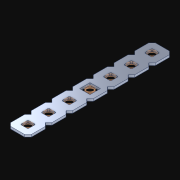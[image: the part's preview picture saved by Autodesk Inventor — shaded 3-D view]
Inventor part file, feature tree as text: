
AUTODESK INVENTOR PART (.ipt)
format: ipt  version: 2021 (Build 250183000, 183)  size: 206,336 bytes
history: native  units: in
note: dims shown in document units (in); Inventor stores cm internally (conversion verified against a paired STEP export)
features: other x8, extrude x7, pattern_linear x1, sketch x1
ambient origin geometry x8: Origin, YZ Plane, XZ Plane, XY Plane, X Axis, Y Axis, Z Axis, Center Point
bodies: Solid1 (feature_tree)
feature tree (17):
  pattern_linear  "Rectangular Pattern1"  Spacing1=1.0in  [1 undecoded]
  sketch  "Sketch1"  dims[d0=0.182in d1=1.0in d2=0.0in d3=2.7559in d5=0.5in]
  other  "Srf1"
  other  "Srf2"
  other  "Srf3"
  other  "Srf4"
  other  "Srf5"
  other  "Srf6"
  other  "Srf7"
  parser-record x1  (decoder bookkeeping rows leaked as tree rows — omitted from the tree; the rows remain in map.json)
  extrude  "ExtrusionSrf1"  Depth=0.5in
  extrude  "ExtrusionSrf2"  [1 undecoded]
  extrude  "ExtrusionSrf3"  [1 undecoded]
  extrude  "ExtrusionSrf4"  [1 undecoded]
  extrude  "ExtrusionSrf5"  [1 undecoded]
  extrude  "ExtrusionSrf6"  [1 undecoded]
  extrude  "ExtrusionSrf7"  [1 undecoded]
note: 7 required parameter values undecoded (feature->parameter linkage not recoverable at this tier; creation-order binding heuristic only, values carry confidence <= 0.55)
